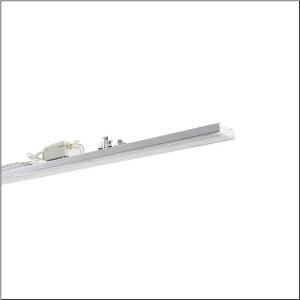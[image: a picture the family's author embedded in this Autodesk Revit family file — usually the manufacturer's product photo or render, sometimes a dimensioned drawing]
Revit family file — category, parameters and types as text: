
# Revit family: licross_21_recessed_mo_52te12dn455g
name_source: partatom
category: Lighting Fixtures
units: mm (PartAtom-declared; Revit-internal decimal feet)

## family parameters
Cut with Voids When Loaded = No
Host = Face
Light Source = No
Part Type = Normal
Room Calculation Point = No
Round Connector Dimension = Use Diameter
Shared = No

## types (1)
- --- (1 x LED, 5510 lm, 29.7 W, 4000K)
    Apparent Load = 30 VA
    CIE Flux Codes = 72 92 99 100 100
    Color Rendering = 80
    Color Temperature = 4000K
    Default Elevation = 1800 mm
    Description = Licross 21 Recessed MO, luminaire insert, of sheet steel, galvanised, coil coated, white, length: 1.500mm, width: 66mm, height: 67mm, LED rated luminous flux: 5.510lm, light colour: 840, SDCM (Standard Deviation of Colour Matching)MacAdam ≤ 3 SDCM (initial), control gear: DALI 2, with plug, 5-pole, with phase selection, mains connection: 220..240V, AC, 50/60Hz, rated input power: 30W, internal wiring halogen-free, primary optical cover: cover, of PMMA, light emission: direct distribution, primary light characteristic: symmetric, protection rating (complete): IP54, insulation class (complete): insulation class I (protective earthing), certification: CE, ENEC, VDE, UKCA, protection symbol: D if used in an environment with non-conductive dust loads with corresponding accessories, impact resistance: IK06, permissible ambient temperature for indoor applications: -25..+45°C, corresponds to IFS (International Featured Standards) requirements for safety and quality in the food industry, reducing of maximum allowable ambient temperature of 5°C with ceiling mounting, LABS conformity tested according to VDMA 24364:2018-05, The light source and the operating device comply with the requirements of the Ecodesign Regulation (EU) 2019/2020 and are replaceable in accordance with this regulation, packaging unit: 1 piece
    Height = 58 mm
    Lamp = 1 x LED
    Lamp Light Flux = 5510 lm
    Lamp Power = 29.7 W
    Lamp count = 1
    Length = 1500 mm
    Luminous efficacy = 186 lm/W
    Manufacturer = Siteco
    ModVariant = No
    Model = 52TE12DN455G
    Mounting Place = Ceiling
    Mounting Type = Pendant
    Number of Poles = 1
    OnlyDefault = Yes
    Power Factor = 1
    Product Name = Licross 21 Recessed MO
    Product group = luminaire insert | ceiling pendant
    ProductGroupID = 901
    Protection Class = Protection class I
    Protection Degree = IP 54
    RLX_Detail_Level = 1
    RLX_Emergency_Light_Flux = 0 lm
    RLX_Emergency_Type = 0
    RLX_Emergency_Type_DB = No
    RlxData = <blob elided: 24317 chars, md5=1eb6f300>
    Socket = socket
    Standby Power = 0 W
    System Light Flux = 5510 lm
    System Power = 30 W
    Type Comments = factory setting: luminous flux: 100 % | dim-lin: 254 | 201 mA
    Type Image = l_1296930.jpg
    URL = http://relux.com
    VarID = @adj_088309
    Voltage = 0 V
    Weight = 0.00 kg
    Width = 66 mm

## geometry (parser evidence)
native form markers: Blend x4, Sweep x10
no freeform markers — native parametric forms only
